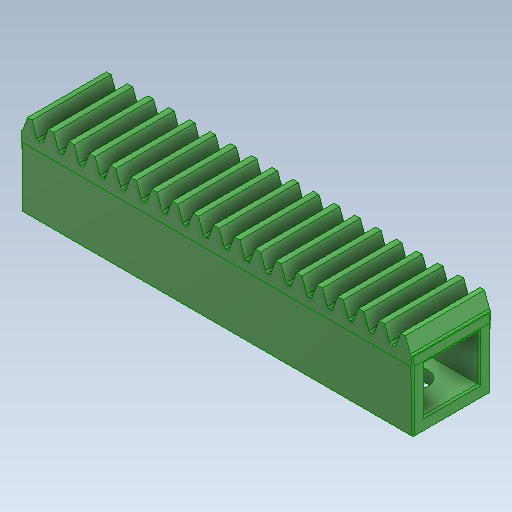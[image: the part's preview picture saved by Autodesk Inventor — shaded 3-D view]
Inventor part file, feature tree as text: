
AUTODESK INVENTOR PART (.ipt)
format: ipt  version: 2020 (Build 240168000, 168)  size: 620,032 bytes
history: native  units: in
note: dims shown in document units (in); Inventor stores cm internally (conversion verified against a paired STEP export)
features: fillet x1
ambient origin geometry x8: Origin, YZ Plane, XZ Plane, XY Plane, X Axis, Y Axis, Z Axis, Center Point
bodies: Solid1 (feature_tree)
feature tree (1):
  fillet  "Fillet11"  [1 undecoded]
note: 1 required parameter value undecoded (feature->parameter linkage not recoverable at this tier; creation-order binding heuristic only, values carry confidence <= 0.55)
